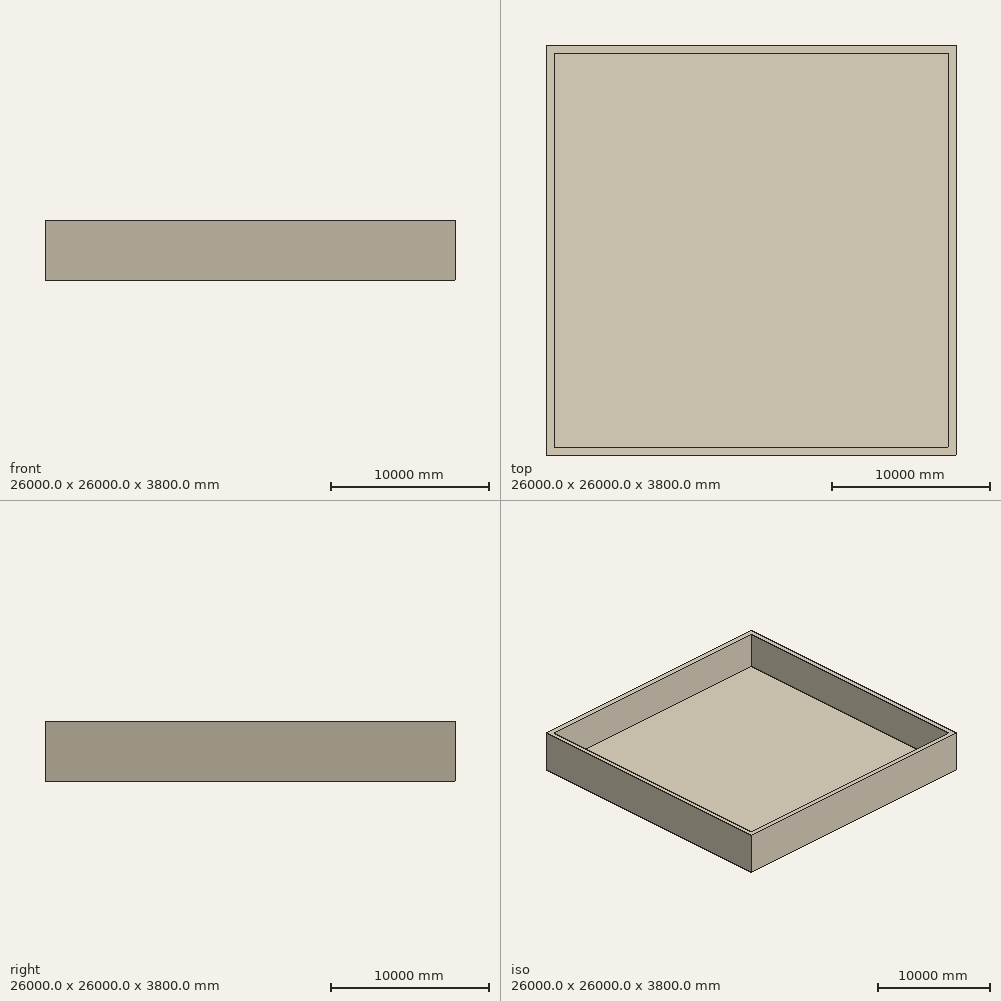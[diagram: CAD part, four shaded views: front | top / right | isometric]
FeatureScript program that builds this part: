
annotation { "Feature Type Name" : "Feature", "Feature Type Description" : "" }
export const myFeature = defineFeature(function(context is Context, id is Id, definition is map)
    precondition{}
    {
        {
            var Q0;
            Q0=qCreatedBy(makeId("Top.planeOp"),FACE);
            var sketch = newSketch(context, id + "F0", { "sketchPlane" : qUnion([Q0])});
            skLineSegment(sketch, "E0.bottom", {"start": v(-13000, 13000) * mm, "end": v(13000, 13000) * mm});
            skLineSegment(sketch, "E0.top", {"start": v(-13000, -13000) * mm, "end": v(13000, -13000) * mm});
            skLineSegment(sketch, "E0.left", {"start": v(-13000, 13000) * mm, "end": v(-13000, -13000) * mm});
            skLineSegment(sketch, "E0.right", {"start": v(13000, 13000) * mm, "end": v(13000, -13000) * mm});
            skLineSegment(sketch, "E1.bottom", {"start": v(-12510, 12510) * mm, "end": v(12510, 12510) * mm});
            skLineSegment(sketch, "E1.top", {"start": v(-12510, -12510) * mm, "end": v(12510, -12510) * mm});
            skLineSegment(sketch, "E1.left", {"start": v(-12510, 12510) * mm, "end": v(-12510, -12510) * mm});
            skLineSegment(sketch, "E1.right", {"start": v(12510, 12510) * mm, "end": v(12510, -12510) * mm});
            skSolve(sketch);
        }
        {
            var Q0;
            Q0=makeQuery(id+"F0.imprint","IMPRINT",FACE,{"disambiguationData":[TD([[makeQuery(id+"F0.imprint","IMPRINT",EDGE,{"derivedFrom":sQuery(id+"F0.wireOp",EDGE,"E0.bottom")}),-1.0]])]});
            extrude(context, id + "F1", {"entities" : qUnion([Q0]), "depth" : 3800 * mm, "offsetDistance" : 25.4 * mm});
        }
        {
            var Q0;
            Q0=qCreatedBy(makeId("Top.planeOp"),FACE);
            var sketch = newSketch(context, id + "F2", { "sketchPlane" : qUnion([Q0])});
            skLineSegment(sketch, "E2.bottom", {"start": v(-12510, 12510) * mm, "end": v(12510, 12510) * mm});
            skLineSegment(sketch, "E2.top", {"start": v(-12510, -12510) * mm, "end": v(12510, -12510) * mm});
            skLineSegment(sketch, "E2.left", {"start": v(-12510, 12510) * mm, "end": v(-12510, -12510) * mm});
            skLineSegment(sketch, "E2.right", {"start": v(12510, 12510) * mm, "end": v(12510, -12510) * mm});
            skSolve(sketch);
        }
        {
            var Q0;
            Q0 = qSketchRegion(id + "F2", true);
            extrude(context, id + "F3", {"entities" : qUnion([Q0]), "operationType" : NewBodyOperationType.ADD, "depth" : 490 * mm, "offsetDistance" : 25.4 * mm});
        }
    });
